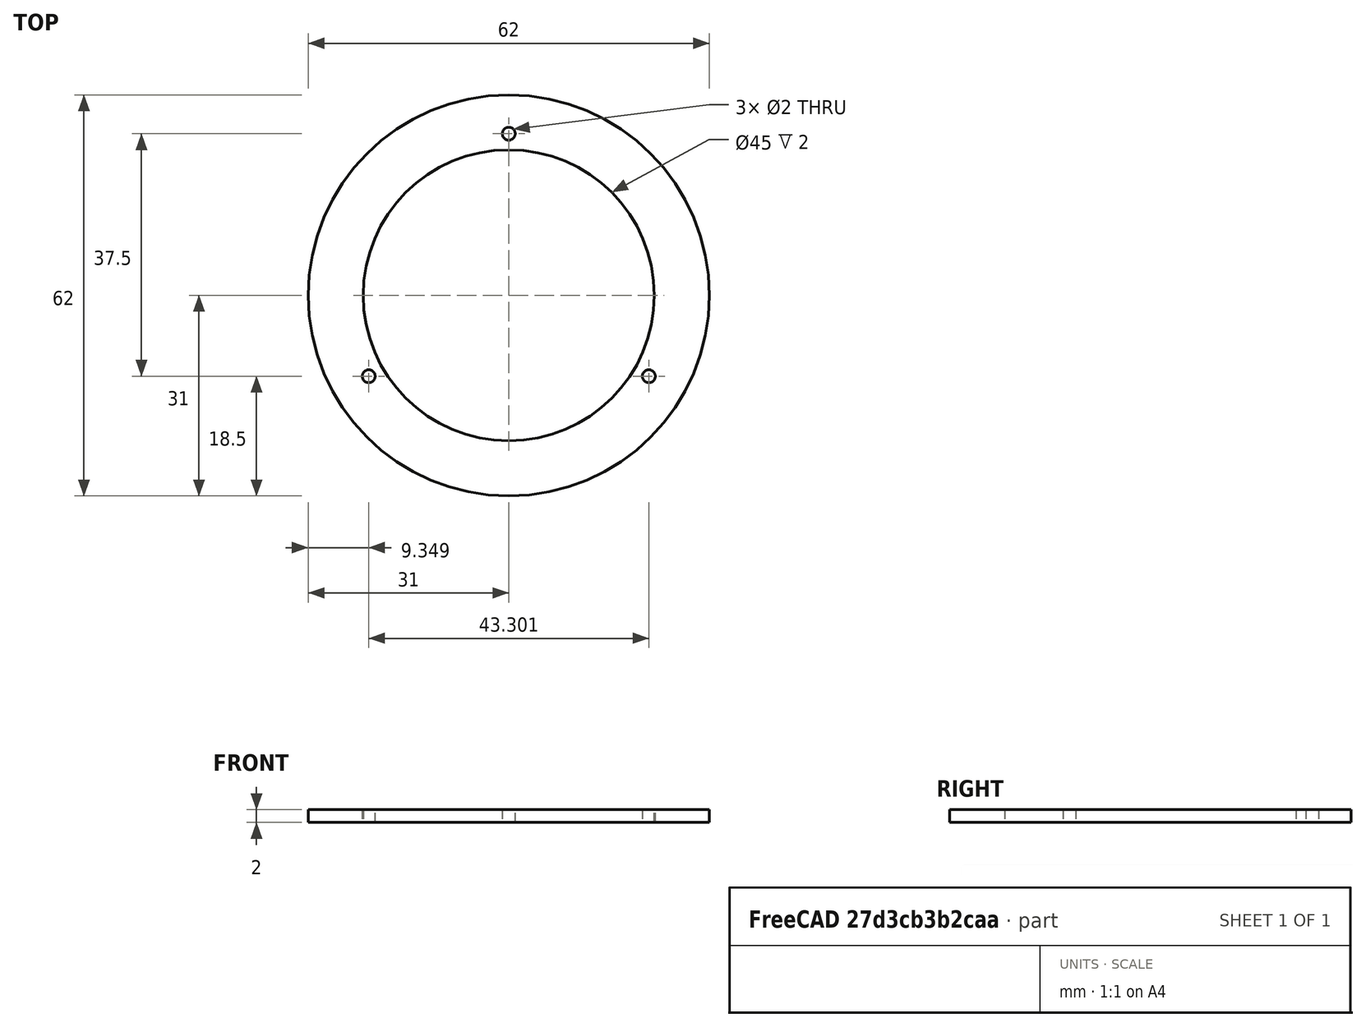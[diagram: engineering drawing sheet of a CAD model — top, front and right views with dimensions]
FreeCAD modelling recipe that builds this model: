
FCSTD DOCUMENT  (FreeCAD 0.19R24276 (Git))
Label: Gt2_d55_cover_3otv
License: All rights reserved
LicenseURL: http://en.wikipedia.org/wiki/All_rights_reserved
objects: Sketcher::SketchObject×1, PartDesign::Pad×1, PartDesign::Body×1
note: 4 computed .brp shape members not serialized (recipe doc carries the construction recipe); baked Part::Feature solids carry a one-line shape summary decoded from their .brp

FEATURE [Sketcher::SketchObject] Sketch  label="Sketch_d45_d62_3otv_on_d50"
  FullyConstrained = true
  MapMode = 5
  Support = -> [XY_Plane]
  sketch-geometry (9):
    g0: Circle CenterX=0 CenterY=0 CenterZ=0 NormalX=0 NormalY=0 NormalZ=1 AngleXU=0 Radius=22.5
    g1: Circle CenterX=0 CenterY=0 CenterZ=0 NormalX=0 NormalY=0 NormalZ=1 AngleXU=0 Radius=31
    g2: LineSegment StartX=0 StartY=25 StartZ=0 EndX=-21.6506 EndY=-12.5 EndZ=0
    g3: LineSegment StartX=-21.6506 StartY=-12.5 StartZ=0 EndX=21.6506 EndY=-12.5 EndZ=0
    g4: LineSegment StartX=21.6506 StartY=-12.5 StartZ=0 EndX=0 EndY=25 EndZ=0
    g5: Circle CenterX=0 CenterY=0 CenterZ=0 NormalX=0 NormalY=0 NormalZ=1 AngleXU=0 Radius=25
    g6: Circle CenterX=0 CenterY=25 CenterZ=0 NormalX=0 NormalY=0 NormalZ=1 AngleXU=0 Radius=1
    g7: Circle CenterX=-21.6506 CenterY=-12.5 CenterZ=0 NormalX=0 NormalY=0 NormalZ=1 AngleXU=0 Radius=1
    g8: Circle CenterX=21.6506 CenterY=-12.5 CenterZ=0 NormalX=0 NormalY=0 NormalZ=1 AngleXU=0 Radius=1
  constraints (21):
    c: Coincident(g0,g-1)
    c: Coincident(g1,g0)
    c: Diameter(g0) = 45
    c: Diameter(g1) = 62
    c: Coincident(g2,g3)
    c: Coincident(g3,g4)
    c: Coincident(g4,g2)
    c: Equal(g2,g3)
    c: Equal(g2,g4)
    c: PointOnObject(g2,g5)
    c: PointOnObject(g3,g5)
    c: PointOnObject(g4,g5)
    c: Coincident(g5,g0)
    c: PointOnObject(g4,g-2)
    c: Diameter(g5) = 50
    c: Coincident(g6,g2)
    c: Coincident(g7,g2)
    c: Coincident(g8,g3)
    c: Diameter(g8) = 2
    c: Equal(g8,g7)
    c: Equal(g8,g6)
FEATURE [PartDesign::Pad] Pad  label="Pad_h2"
  Direction = (1,1,1)
  Length = 2
  Length2 = 100
  Profile = -> Sketch
  Type = 0
FEATURE [PartDesign::Body] Body
  Group = -> [Sketch,Pad]
  Origin = -> Origin
  Tip = -> Pad
